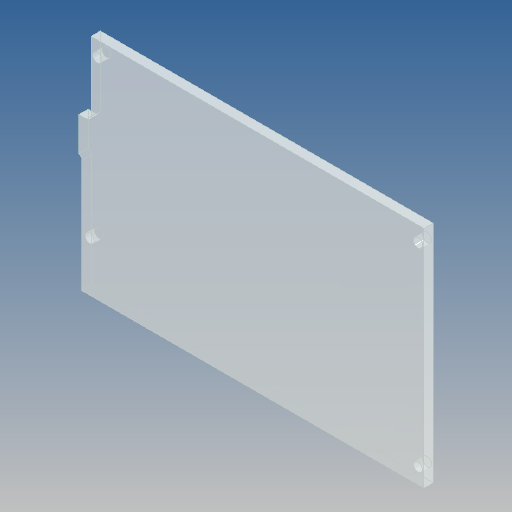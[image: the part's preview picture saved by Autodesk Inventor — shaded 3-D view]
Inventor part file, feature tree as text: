
AUTODESK INVENTOR PART (.ipt)
format: ipt  version: 2020 (Build 240168000, 168)  size: 161,280 bytes
history: native  units: mm
features: reference x8, sketch x3, extrude x2, other x2, hole x1, fillet x1
ambient origin geometry x8: Origin, YZ Plane, XZ Plane, XY Plane, X Axis, Y Axis, Z Axis, Center Point
bodies: Solid1 (feature_tree)
feature tree (17):
  extrude  "Extrusion1"  Depth=73.0mm
  extrude  "Extrusion2"  Depth=3.0mm
  hole  "Hole1"  [1 undecoded]
  fillet  "Fillet1"  Radius=0.5mm
  sketch  "Sketch1"  dims[d0=108.0mm d1=73.0mm]
  sketch  "Sketch2"  dims[d2=3.0mm d3=0.0mm d5=0.5mm]
  reference  "Reference1"
  reference  "Reference2"
  reference  "Reference3"
  reference  "Reference4"
  sketch  "Sketch3"  dims[d6=0.5mm d7=0.5mm d8=0.5mm d9=3.0mm d10=0.0mm d11=3.0mm d12=6.0mm d13=4.0mm d14=2.0mm d15=90.0deg d16=8.0mm d17=20.594885mm d18=1.5mm]
  reference  "Reference5"
  reference  "Reference6"
  reference  "Reference7"
  reference  "Reference8"
  other  "30-00 Injectomat suplimentar.iam"
  other  "0008-30-002 Corp_Injectomat1:1"
note: 1 required parameter value undecoded (feature->parameter linkage not recoverable at this tier; creation-order binding heuristic only, values carry confidence <= 0.55)
